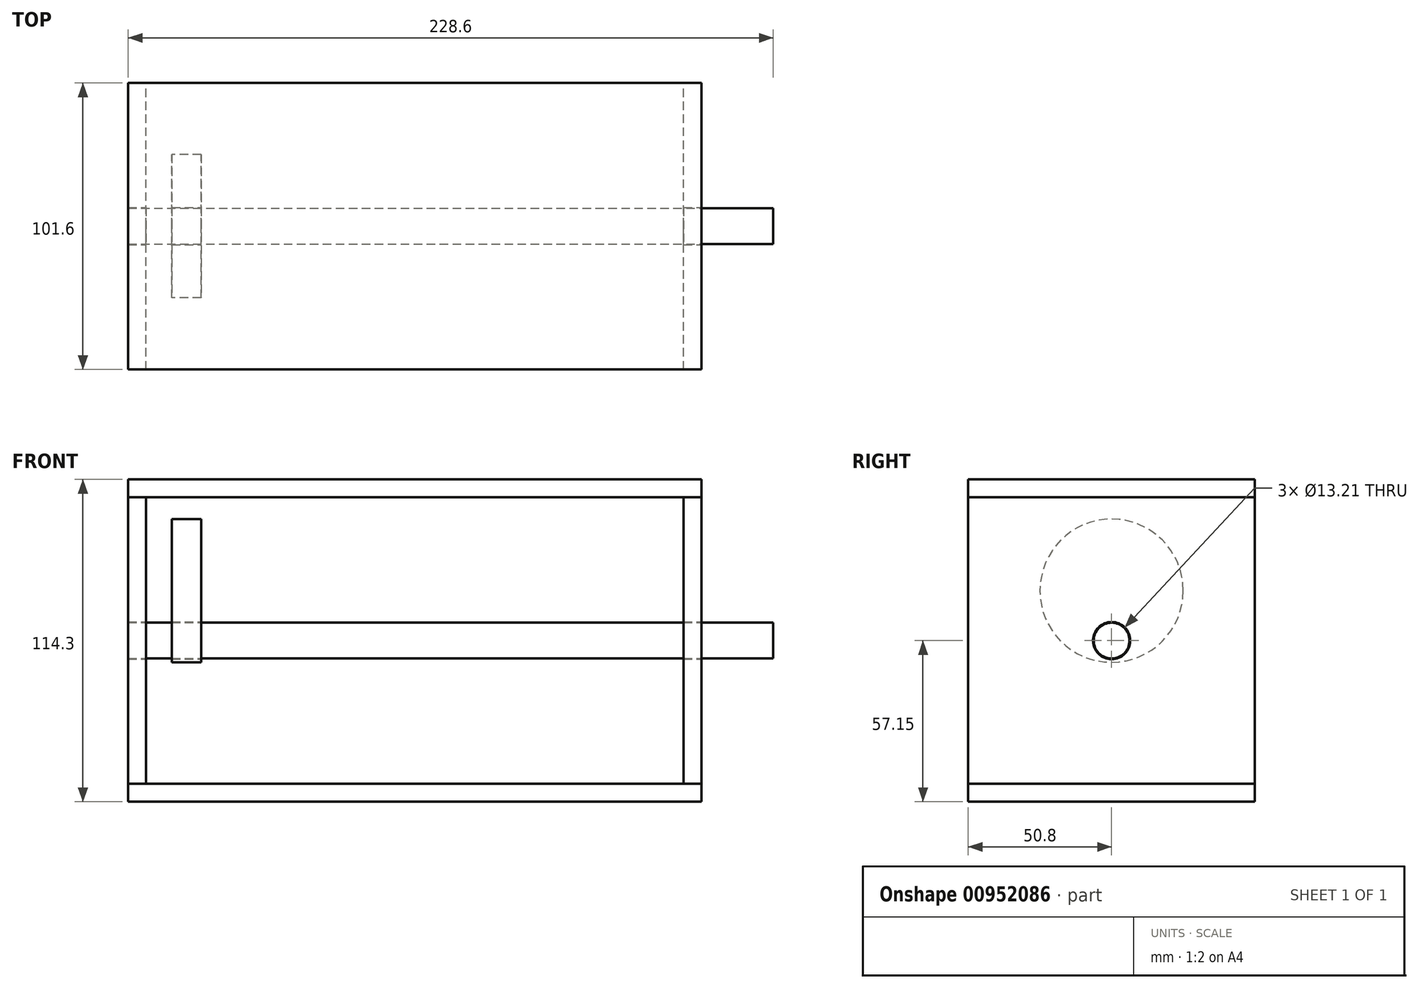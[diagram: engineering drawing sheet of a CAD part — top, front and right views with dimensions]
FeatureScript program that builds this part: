
annotation { "Feature Type Name" : "Feature", "Feature Type Description" : "" }
export const myFeature = defineFeature(function(context is Context, id is Id, definition is map)
    precondition{}
    {
        {
            var Q0;
            Q0=qCreatedBy(makeId("Front.planeOp"),FACE);
            var sketch = newSketch(context, id + "F0", { "sketchPlane" : qUnion([Q0])});
            skLineSegment(sketch, "E0", {"start": v(-101.6, 0) * mm, "end": v(101.6, 0) * mm});
            skLineSegment(sketch, "E1", {"start": v(-101.6, 6.35) * mm, "end": v(-101.6, 0) * mm});
            skLineSegment(sketch, "E2", {"start": v(101.6, 6.35) * mm, "end": v(101.6, 0) * mm});
            skLineSegment(sketch, "E3", {"start": v(-101.6, 6.35) * mm, "end": v(101.6, 6.35) * mm});
            skLineSegment(sketch, "E4", {"start": v(-101.6, 114.3) * mm, "end": v(101.6, 114.3) * mm});
            skLineSegment(sketch, "E5", {"start": v(-101.6, 107.95) * mm, "end": v(101.6, 107.95) * mm});
            skLineSegment(sketch, "E6", {"start": v(-101.6, 114.3) * mm, "end": v(-101.6, 107.95) * mm});
            skLineSegment(sketch, "E7", {"start": v(-101.6, 107.95) * mm, "end": v(-101.6, 6.35) * mm});
            skLineSegment(sketch, "E8", {"start": v(101.6, 107.95) * mm, "end": v(101.6, 114.3) * mm});
            skLineSegment(sketch, "E9", {"start": v(101.6, 107.95) * mm, "end": v(101.6, 6.35) * mm});
            skLineSegment(sketch, "E10", {"start": v(95.25, 107.95) * mm, "end": v(95.25, 6.35) * mm});
            skLineSegment(sketch, "E11", {"start": v(95.25, 57.15) * mm, "end": v(101.6, 57.15) * mm, "construction": true});
            skLineSegment(sketch, "E12", {"start": v(-95.25, 107.95) * mm, "end": v(-95.25, 6.35) * mm});
            skLineSegment(sketch, "E13", {"start": v(-95.25, 57.15) * mm, "end": v(-101.6, 57.15) * mm, "construction": true});
            skLineSegment(sketch, "E14.bottom", {"start": v(-86.13, 100.27) * mm, "end": v(-75.73, 100.27) * mm});
            skLineSegment(sketch, "E14.top", {"start": v(-86.13, 49.47) * mm, "end": v(-75.73, 49.47) * mm});
            skLineSegment(sketch, "E14.left", {"start": v(-86.13, 100.27) * mm, "end": v(-86.13, 49.47) * mm});
            skLineSegment(sketch, "E14.right", {"start": v(-75.73, 100.27) * mm, "end": v(-75.73, 49.47) * mm});
            skLineSegment(sketch, "E15", {"start": v(-86.13, 74.87) * mm, "end": v(-75.73, 74.87) * mm});
            skLineSegment(sketch, "E16", {"start": v(-95.25, 57.15) * mm, "end": v(95.25, 57.15) * mm});
            skLineSegment(sketch, "E17", {"start": v(-80.93, 100.27) * mm, "end": v(-80.93, 114.3) * mm, "construction": true});
            skSolve(sketch);
        }
        {
            var Q0;
            Q0=makeQuery(id+"F0.imprint","IMPRINT",FACE,{"disambiguationData":[TD([[makeQuery(id+"F0.imprint","IMPRINT",EDGE,{"derivedFrom":sQuery(id+"F0.wireOp",EDGE,"E4")}),-1.0]])]});
            var Q1;
            Q1=makeQuery(id+"F0.imprint","IMPRINT",FACE,{"disambiguationData":[TD([[makeQuery(id+"F0.imprint","IMPRINT",EDGE,{"derivedFrom":sQuery(id+"F0.wireOp",EDGE,"E0")}),1.0]])]});
            extrude(context, id + "F1", {"entities" : qUnion([Q0, Q1]), "endBound" : BoundingType.SYMMETRIC, "depth" : 101.6 * mm, "offsetDistance" : 25.4 * mm, "hasSecondDirection" : true, "secondDirectionOppositeDirection" : true, "secondDirectionDepth" : 50.8 * mm});
        }
        {
            var Q0;
            {var subQ0=sQuery(id+"F0.wireOp",EDGE,"E7");Q0=makeQuery(id+"F0.imprint","IMPRINT",FACE,{"disambiguationData":[TD([[makeQuery(id+"F0.imprint","IMPRINT",EDGE,{"derivedFrom":subQ0}),1.0]])]});}
            var Q1;
            {var subQ0=sQuery(id+"F0.wireOp",EDGE,"E9");Q1=makeQuery(id+"F0.imprint","IMPRINT",FACE,{"disambiguationData":[TD([[makeQuery(id+"F0.imprint","IMPRINT",EDGE,{"derivedFrom":subQ0}),-1.0]])]});}
            var Q2;
            Q2=makeQuery(id+"F1.opExtrude","CAP_FACE",FACE,{"disambiguationData":[OSD([sQuery(id+"F0.wireOp",EDGE,"E0"),sQuery(id+"F0.wireOp",EDGE,"E1"),sQuery(id+"F0.wireOp",EDGE,"E2"),sQuery(id+"F0.wireOp",EDGE,"E3")])],"isStart":false});
            var Q3;
            Q3=makeQuery(id+"F1.opExtrude","CAP_FACE",FACE,{"disambiguationData":[OSD([sQuery(id+"F0.wireOp",EDGE,"E0"),sQuery(id+"F0.wireOp",EDGE,"E1"),sQuery(id+"F0.wireOp",EDGE,"E2"),sQuery(id+"F0.wireOp",EDGE,"E3")])],"isStart":true});
            extrude(context, id + "F2", {"entities" : qUnion([Q0, Q1]), "endBound" : BoundingType.UP_TO_SURFACE, "depth" : 101.6 * mm, "endBoundEntityFace" : qUnion([Q2]), "offsetDistance" : 25.4 * mm, "hasSecondDirection" : true, "secondDirectionBound" : SecondDirectionBoundingType.UP_TO_SURFACE, "secondDirectionOppositeDirection" : true, "secondDirectionDepth" : 25.4 * mm, "secondDirectionBoundEntityFace" : qUnion([Q3])});
        }
        {
            var Q0;
            {var subQ0=sQuery(id+"F0.wireOp",EDGE,"E14.bottom");Q0=makeQuery(id+"F0.imprint","IMPRINT",FACE,{"disambiguationData":[TD([[makeQuery(id+"F0.imprint","IMPRINT",EDGE,{"derivedFrom":subQ0}),-1.0]])]});}
            var Q1;
            Q1=sQuery(id+"F0.wireOp",EDGE,"E15");
            revolve(context, id + "F3", {"surfaceOperationType" : NewSurfaceOperationType.NEW, "entities" : qUnion([Q0]), "axis" : qUnion([Q1]), "revolveType" : RevolveType.FULL});
        }
        {
            var Q0;
            Q0=makeQuery(id+"F2.opExtrude","SWEPT_FACE",FACE,{"disambiguationData":[OSD([sQuery(id+"F0.wireOp",EDGE,"E9")])]});
            var sketch = newSketch(context, id + "F4", { "sketchPlane" : qUnion([Q0])});
            skCircle(sketch, "E18", {"center": v(0, 57.15) * mm, "radius": 6.35 * mm});
            skCircle(sketch, "E19", {"center": v(0, 57.15) * mm, "radius": 6.6 * mm});
            skSolve(sketch);
        }
        {
            var Q0;
            Q0=makeQuery(id+"F4.imprint","IMPRINT",FACE,{"disambiguationData":[TD([[makeQuery(id+"F4.imprint","IMPRINT",EDGE,{"derivedFrom":sQuery(id+"F4.wireOp",EDGE,"E18")}),1.0]])]});
            var Q1;
            Q1=makeQuery(id+"F4.imprint","IMPRINT",FACE,{"disambiguationData":[TD([[makeQuery(id+"F4.imprint","IMPRINT",EDGE,{"derivedFrom":sQuery(id+"F4.wireOp",EDGE,"E18")}),-1.0]])]});
            extrude(context, id + "F5", {"entities" : qUnion([Q0, Q1]), "operationType" : NewBodyOperationType.REMOVE, "endBound" : BoundingType.THROUGH_ALL, "oppositeDirection" : true, "depth" : 25.4 * mm, "offsetDistance" : 25.4 * mm});
        }
        {
            var Q0;
            Q0=makeQuery(id+"F4.imprint","IMPRINT",FACE,{"disambiguationData":[TD([[makeQuery(id+"F4.imprint","IMPRINT",EDGE,{"derivedFrom":sQuery(id+"F4.wireOp",EDGE,"E18")}),1.0]])]});
            var Q1;
            Q1=makeQuery(id+"F2.opExtrude","SWEPT_FACE",FACE,{"disambiguationData":[OSD([sQuery(id+"F0.wireOp",EDGE,"E7")])]});
            extrude(context, id + "F6", {"entities" : qUnion([Q0]), "endBound" : BoundingType.UP_TO_SURFACE, "oppositeDirection" : true, "depth" : 25.4 * mm, "endBoundEntityFace" : qUnion([Q1]), "offsetDistance" : 25.4 * mm, "hasSecondDirection" : true, "secondDirectionOppositeDirection" : false, "secondDirectionDepth" : 25.4 * mm});
        }
        {
            var Q0;
            Q0=makeQuery(id+"F6.opExtrude","SWEPT_BODY",BODY,{"disambiguationData":[OSD([sQuery(id+"F4.wireOp",EDGE,"E18")])]});
            var Q1;
            Q1=makeQuery(id+"F3.opRevolve","SWEPT_BODY",BODY,{"disambiguationData":[OSD([sQuery(id+"F0.wireOp",EDGE,"E14.bottom"),sQuery(id+"F0.wireOp",EDGE,"E14.left"),sQuery(id+"F0.wireOp",EDGE,"E14.right"),sQuery(id+"F0.wireOp",EDGE,"E15")])]});
            booleanBodies(context, id + "F7", {"operationType" : BooleanOperationType.SUBTRACTION, "tools" : qUnion([Q0]), "targets" : qUnion([Q1]), "keepTools" : true});
        }
    });
